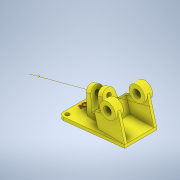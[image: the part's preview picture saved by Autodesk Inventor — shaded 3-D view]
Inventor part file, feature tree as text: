
AUTODESK INVENTOR PART (.ipt)
format: ipt  version: 2022 (Build 260153000, 153)  size: 336,384 bytes
history: native  units: mm
features: sketch x13, extrude x7, hole x4, other x2, emboss x1
ambient origin geometry x8: Origin, YZ Plane, XZ Plane, XY Plane, X Axis, Y Axis, Z Axis, Center Point
bodies: Solid1 (feature_tree)
feature tree (27):
  other  "Work Axis1"
  sketch  "Sketch1"  dims[d21=12.0mm d22=9.0mm]
  extrude  "Extrusion1"  Depth=9.0mm
  extrude  "Extrusion2"  Depth=35.0mm
  extrude  "Extrusion3"  Depth=50.0mm TaperAngle=0.0deg
  extrude  "Extrusion4"  Depth=13.613568mm
  extrude  "Extrusion5"  Depth=15.0mm
  extrude  "Extrusion6"  Depth=5.0mm
  extrude  "Extrusion7"  Depth=49.0mm
  hole  "Hole1"  [1 undecoded]
  hole  "Hole2"  [1 undecoded]
  hole  "Hole3"  [1 undecoded]
  hole  "Hole4"  [1 undecoded]
  emboss  "Emboss1"
  other  "Work Point1"
  sketch  "Sketch3"  dims[d23=117.0mm d24=35.0mm]
  sketch  "Sketch4"  dims[d25=14.0mm d26=50.0mm d27=0.0mm]
  sketch  "Sketch5"  dims[d28=12.0mm d29=13.613568mm]
  sketch  "Sketch6"  dims[d30=13.613568mm d31=15.0mm]
  sketch  "Sketch7"  dims[d32=0.0mm d33=0.0mm d34=5.0mm]
  sketch  "Sketch8"  dims[d35=25.3mm d36=49.0mm]
  sketch  "Sketch9"  dims[d37=30.0mm d38=61.0mm d39=0.0mm]
  sketch  "Sketch10"  dims[d40=5.0mm d41=5.0mm]
  sketch  "Sketch11"  dims[d42=5.0mm d43=5.0mm]
  sketch  "Sketch12"  dims[d44=61.0mm d45=0.0mm d46=71.0mm d47=0.0mm]
  sketch  "Sketch13"  dims[d48=39.0mm]
  sketch  "Sketch14"  dims[d49=41.0mm d50=0.0mm d51=8.0mm d52=113.0mm d53=70.0mm d54=35.0mm d55=6.0mm d56=0.0mm d57=15.0mm d58=6.0mm d59=4.0mm d60=2.0mm d61=90.0deg d62=8.0mm d63=0.0mm d64=8.0mm d65=6.0mm d66=4.0mm d67=2.0mm d68=90.0deg d69=8.0mm d70=0.0mm d71=8.0mm d72=6.0mm d73=4.0mm d74=2.0mm d75=90.0deg d76=8.0mm d77=0.0mm d78=9.0mm d79=6.0mm d80=4.0mm d81=2.0mm d82=90.0deg d83=8.0mm d84=0.0mm d85=15.0mm d86=29.0mm d87=11.0mm d88=1.0mm d89=0.0mm]
note: 4 required parameter values undecoded (feature->parameter linkage not recoverable at this tier; creation-order binding heuristic only, values carry confidence <= 0.55)
